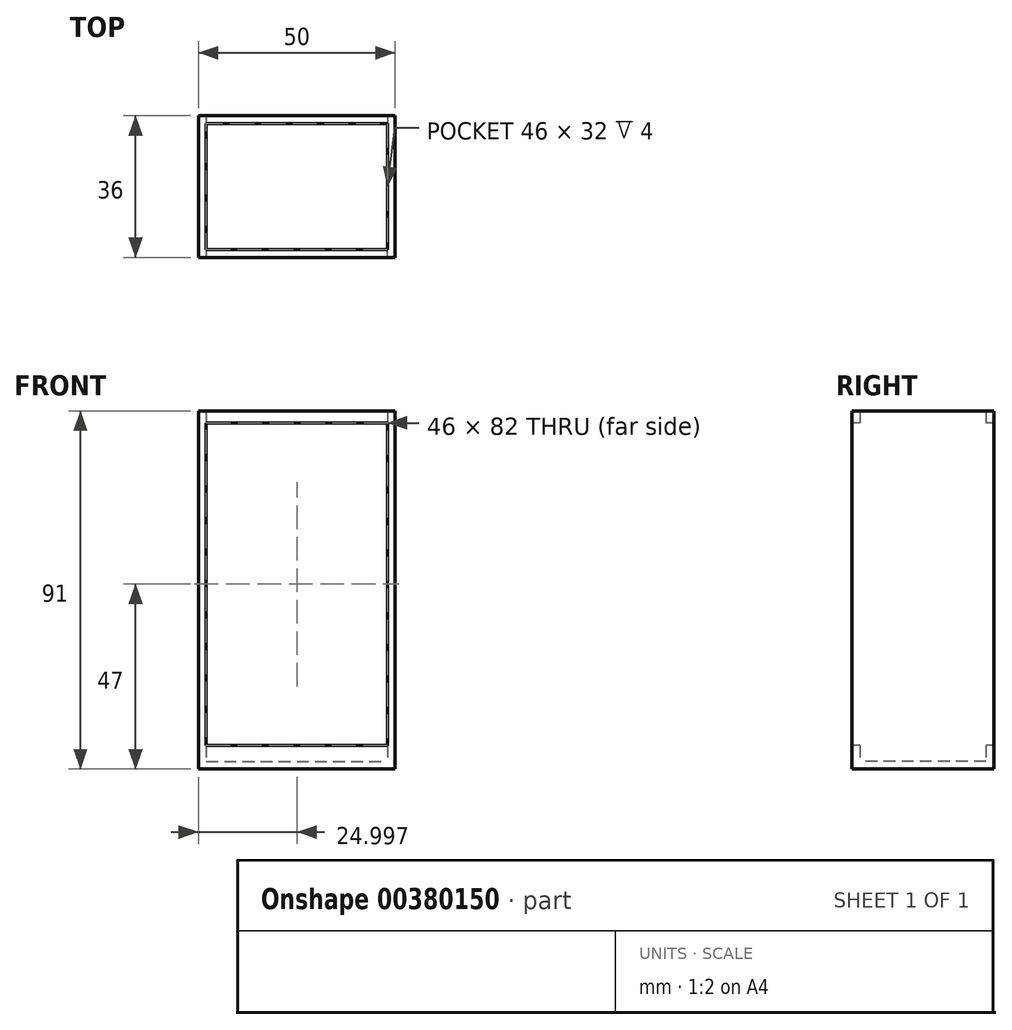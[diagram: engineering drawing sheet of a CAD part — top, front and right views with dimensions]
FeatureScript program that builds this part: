
annotation { "Feature Type Name" : "Feature", "Feature Type Description" : "" }
export const myFeature = defineFeature(function(context is Context, id is Id, definition is map)
    precondition{}
    {
        {
            var Q0;
            Q0=qCreatedBy(makeId("Top.planeOp"),FACE);
            var sketch = newSketch(context, id + "F0", { "sketchPlane" : qUnion([Q0])});
            skLineSegment(sketch, "E0.bottom", {"start": v(-57.9, 42.38) * mm, "end": v(-7.9, 42.38) * mm});
            skLineSegment(sketch, "E0.top", {"start": v(-57.9, 6.38) * mm, "end": v(-7.9, 6.38) * mm});
            skLineSegment(sketch, "E0.left", {"start": v(-57.9, 42.38) * mm, "end": v(-57.9, 6.38) * mm});
            skLineSegment(sketch, "E0.right", {"start": v(-7.9, 42.38) * mm, "end": v(-7.9, 6.38) * mm});
            skSolve(sketch);
        }
        {
            var Q0;
            Q0=qSketchRegion(id+"F0",true);
            extrude(context, id + "F1", {"entities" : qUnion([Q0]), "depth" : 2 * mm});
        }
        {
            var Q0;
            Q0=makeQuery(id+"F1.opExtrude","CAP_FACE",FACE,{"disambiguationData":[OSD([sQuery(id+"F0.wireOp",EDGE,"E0.bottom"),sQuery(id+"F0.wireOp",EDGE,"E0.top"),sQuery(id+"F0.wireOp",EDGE,"E0.left"),sQuery(id+"F0.wireOp",EDGE,"E0.right")])],"isStart":false});
            var sketch = newSketch(context, id + "F2", { "sketchPlane" : qUnion([Q0])});
            skLineSegment(sketch, "E1.bottom", {"start": v(-57.9, 42.38) * mm, "end": v(-7.9, 42.38) * mm});
            skLineSegment(sketch, "E1.top", {"start": v(-57.9, 6.38) * mm, "end": v(-7.9, 6.38) * mm});
            skLineSegment(sketch, "E1.left", {"start": v(-57.9, 42.38) * mm, "end": v(-57.9, 6.38) * mm});
            skLineSegment(sketch, "E1.right", {"start": v(-7.9, 42.38) * mm, "end": v(-7.9, 6.38) * mm});
            skLineSegment(sketch, "E2.bottom", {"start": v(-55.9, 40.38) * mm, "end": v(-9.9, 40.38) * mm});
            skLineSegment(sketch, "E2.top", {"start": v(-55.9, 8.38) * mm, "end": v(-9.9, 8.38) * mm});
            skLineSegment(sketch, "E2.left", {"start": v(-55.9, 40.38) * mm, "end": v(-55.9, 8.38) * mm});
            skLineSegment(sketch, "E2.right", {"start": v(-9.9, 40.38) * mm, "end": v(-9.9, 8.38) * mm});
            skSolve(sketch);
        }
        {
            var Q0;
            Q0=qSketchRegion(id+"F2",true);
            extrude(context, id + "F3", {"entities" : qUnion([Q0]), "operationType" : NewBodyOperationType.ADD, "depth" : 4 * mm});
        }
        {
            var Q0;
            Q0=makeQuery(id+"F3.opExtrude","CAP_FACE",FACE,{"disambiguationData":[OSD([sQuery(id+"F2.wireOp",EDGE,"E1.bottom"),sQuery(id+"F2.wireOp",EDGE,"E1.top"),sQuery(id+"F2.wireOp",EDGE,"E1.left"),sQuery(id+"F2.wireOp",EDGE,"E1.right"),sQuery(id+"F2.wireOp",EDGE,"E2.bottom"),sQuery(id+"F2.wireOp",EDGE,"E2.top"),sQuery(id+"F2.wireOp",EDGE,"E2.left"),sQuery(id+"F2.wireOp",EDGE,"E2.right")])],"isStart":false});
            var sketch = newSketch(context, id + "F4", { "sketchPlane" : qUnion([Q0])});
            skLineSegment(sketch, "E3.bottom", {"start": v(-57.9, 6.38) * mm, "end": v(-55.9, 6.38) * mm});
            skLineSegment(sketch, "E3.top", {"start": v(-57.9, 42.38) * mm, "end": v(-55.9, 42.38) * mm});
            skLineSegment(sketch, "E3.left", {"start": v(-57.9, 6.38) * mm, "end": v(-57.9, 42.38) * mm});
            skLineSegment(sketch, "E3.right", {"start": v(-55.9, 6.38) * mm, "end": v(-55.9, 42.38) * mm});
            skLineSegment(sketch, "E4.bottom", {"start": v(-9.9, 6.38) * mm, "end": v(-7.9, 6.38) * mm});
            skLineSegment(sketch, "E4.top", {"start": v(-9.9, 42.38) * mm, "end": v(-7.9, 42.38) * mm});
            skLineSegment(sketch, "E4.left", {"start": v(-9.9, 6.38) * mm, "end": v(-9.9, 42.38) * mm});
            skLineSegment(sketch, "E4.right", {"start": v(-7.9, 6.38) * mm, "end": v(-7.9, 42.38) * mm});
            skSolve(sketch);
        }
        {
            var Q0;
            Q0=qSketchRegion(id+"F4",true);
            extrude(context, id + "F5", {"entities" : qUnion([Q0]), "operationType" : NewBodyOperationType.ADD, "depth" : 85 * mm});
        }
        {
            var Q0;
            Q0=makeQuery(id+"F5.opExtrude","CAP_FACE",FACE,{"disambiguationData":[OSD([sQuery(id+"F4.wireOp",EDGE,"E3.bottom"),sQuery(id+"F4.wireOp",EDGE,"E3.top"),sQuery(id+"F4.wireOp",EDGE,"E3.left"),sQuery(id+"F4.wireOp",EDGE,"E3.right")])],"isStart":false});
            var sketch = newSketch(context, id + "F6", { "sketchPlane" : qUnion([Q0])});
            skLineSegment(sketch, "E5.bottom", {"start": v(-57.9, 42.38) * mm, "end": v(-7.9, 42.38) * mm});
            skLineSegment(sketch, "E5.top", {"start": v(-57.9, 6.38) * mm, "end": v(-7.9, 6.38) * mm});
            skLineSegment(sketch, "E5.left", {"start": v(-57.9, 42.38) * mm, "end": v(-57.9, 6.38) * mm});
            skLineSegment(sketch, "E5.right", {"start": v(-7.9, 42.38) * mm, "end": v(-7.9, 6.38) * mm});
            skSolve(sketch);
        }
        {
            var Q0;
            Q0=qSketchRegion(id+"F6",true);
            extrude(context, id + "F7", {"entities" : qUnion([Q0]), "operationType" : NewBodyOperationType.ADD, "oppositeDirection" : true, "depth" : 3 * mm});
        }
        {
            var Q0;
            Q0=makeQuery(id+"F7.opExtrude","CAP_FACE",FACE,{"disambiguationData":[OSD([sQuery(id+"F6.wireOp",EDGE,"E5.bottom"),sQuery(id+"F6.wireOp",EDGE,"E5.top"),sQuery(id+"F6.wireOp",EDGE,"E5.left"),sQuery(id+"F6.wireOp",EDGE,"E5.right")])],"isStart":false});
            var sketch = newSketch(context, id + "F8", { "sketchPlane" : qUnion([Q0])});
            skLineSegment(sketch, "E6.bottom", {"start": v(-55.9, -8.38) * mm, "end": v(-9.9, -8.38) * mm});
            skLineSegment(sketch, "E6.top", {"start": v(-55.9, -40.38) * mm, "end": v(-9.9, -40.38) * mm});
            skLineSegment(sketch, "E6.left", {"start": v(-55.9, -8.38) * mm, "end": v(-55.9, -40.38) * mm});
            skLineSegment(sketch, "E6.right", {"start": v(-9.9, -8.38) * mm, "end": v(-9.9, -40.38) * mm});
            skSolve(sketch);
        }
        {
            var Q0;
            Q0=qSketchRegion(id+"F8",true);
            extrude(context, id + "F9", {"entities" : qUnion([Q0]), "operationType" : NewBodyOperationType.REMOVE, "oppositeDirection" : true, "depth" : 25 * mm});
        }
    });
